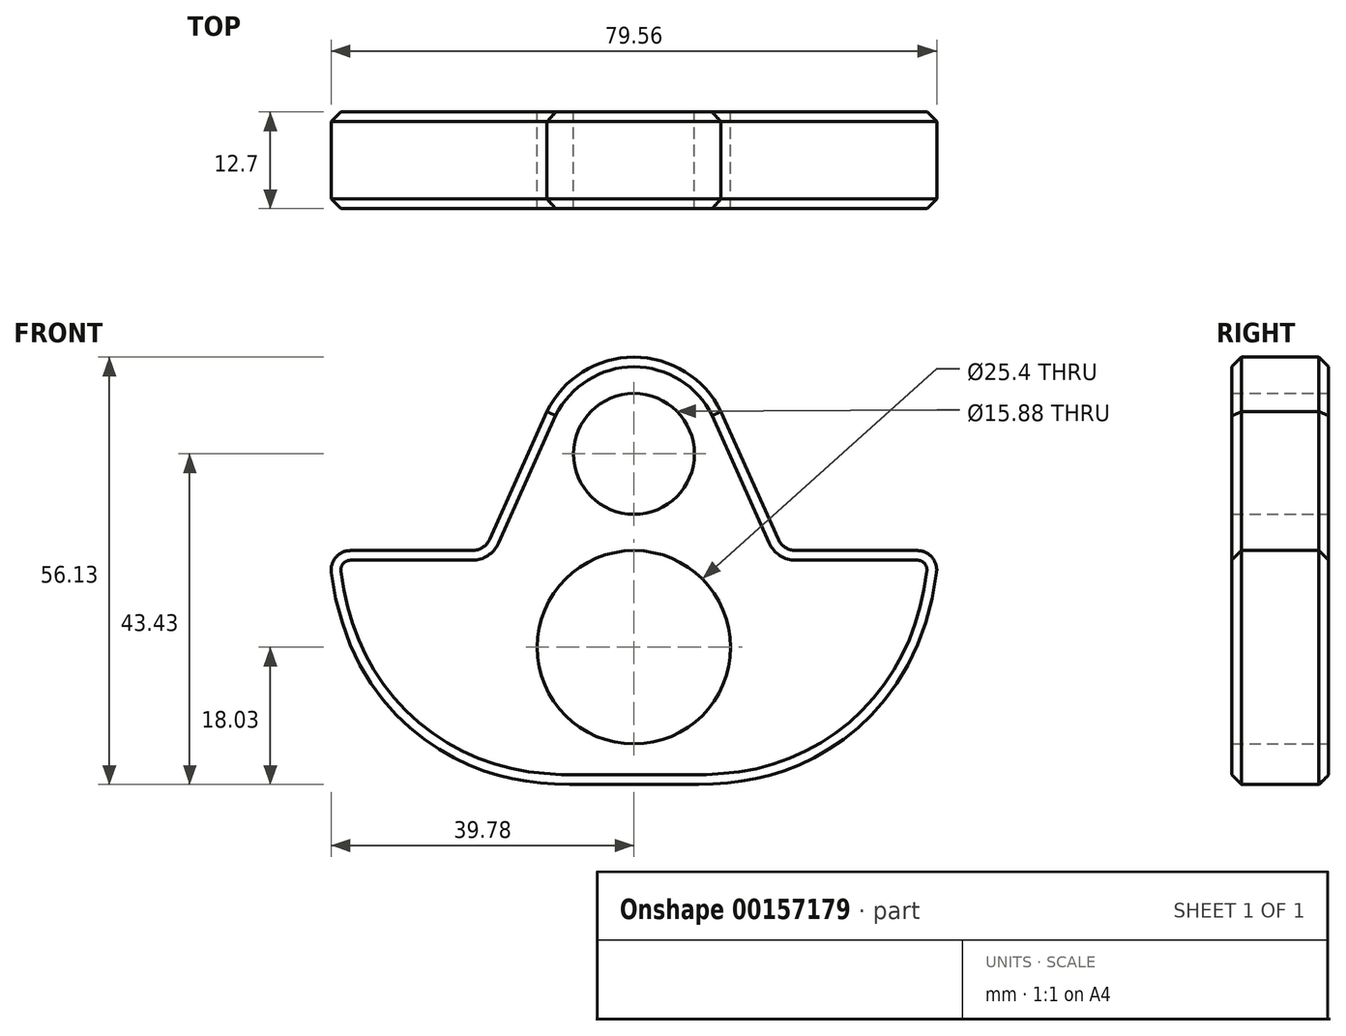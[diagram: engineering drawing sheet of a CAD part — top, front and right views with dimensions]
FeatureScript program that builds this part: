
annotation { "Feature Type Name" : "Feature", "Feature Type Description" : "" }
export const myFeature = defineFeature(function(context is Context, id is Id, definition is map)
    precondition{}
    {
        {
            var Q0;
            Q0=qCreatedBy(makeId("Front.planeOp"),FACE);
            var sketch = newSketch(context, id + "F0", { "sketchPlane" : qUnion([Q0])});
            skCircle(sketch, "E0", {"center": v(0, 0) * mm, "radius": 12.7 * mm});
            skLineSegment(sketch, "E1", {"start": v(0, 0) * mm, "end": v(0, 25.4) * mm});
            skCircle(sketch, "E2", {"center": v(0, 25.4) * mm, "radius": 7.94 * mm});
            skFitSpline(sketch, "E3", {"points": [v(0, -18) * mm, v(20.39, -15.98) * mm, v(40.02, 12.7) * mm], "startDerivative": vector(55.15, 0.13) * mm, "endDerivative": vector(5.47, 90.1) * mm});
            skLineSegment(sketch, "E4", {"start": v(37.24, 12.7) * mm, "end": v(21.26, 12.7) * mm});
            skArc(sketch, "E5", {"start": v(11.74, 30.24) * mm, "mid": v(0, 38.1) * mm, "end": v(-11.74, 30.24) * mm});
            skLineSegment(sketch, "E6", {"start": v(18.95, 14.2) * mm, "end": v(11.42, 30.96) * mm});
            skArc(sketch, "E7.filletArc", {"start": v(39.76, 9.84) * mm, "mid": v(39.14, 11.84) * mm, "end": v(37.24, 12.7) * mm});
            skPoint(sketch, "E8.visualSharp", {"position": v(19.62, 12.7) * mm});
            skArc(sketch, "E8.filletArc", {"start": v(18.95, 14.2) * mm, "mid": v(19.88, 13.1) * mm, "end": v(21.26, 12.7) * mm});
            skLineSegment(sketch, "E9.MirrorCS", {"start": v(-18.95, 14.2) * mm, "end": v(-11.42, 30.96) * mm});
            skLineSegment(sketch, "E10.MirrorCS", {"start": v(-37.24, 12.7) * mm, "end": v(-21.26, 12.7) * mm});
            skArc(sketch, "E11.MirrorCS", {"start": v(-18.95, 14.2) * mm, "mid": v(-19.88, 13.1) * mm, "end": v(-21.26, 12.7) * mm});
            skArc(sketch, "E12.MirrorCS", {"start": v(-39.76, 9.84) * mm, "mid": v(-39.14, 11.84) * mm, "end": v(-37.24, 12.7) * mm});
            skFitSpline(sketch, "E13.MirrorCS", {"points": [v(0, -18) * mm, v(-20.39, -15.98) * mm, v(-40.02, 12.7) * mm], "startDerivative": vector(-55.15, 0.13) * mm, "endDerivative": vector(-5.47, 90.1) * mm});
            skSolve(sketch);
        }
        {
            var Q0;
            Q0=makeQuery(id+"F0.imprint","IMPRINT",FACE,{"disambiguationData":[TD([[makeQuery(id+"F0.imprint","IMPRINT",EDGE,{"derivedFrom":sQuery(id+"F0.wireOp",EDGE,"E0")}),-1.0]])]});
            extrude(context, id + "F1", {"entities" : qUnion([Q0]), "depth" : 12.7 * mm});
        }
        {
            var Q0;
            Q0=makeQuery(id+"F1.opExtrude","CAP_EDGE",EDGE,{"disambiguationData":[OSD([sQuery(id+"F0.wireOp",EDGE,"E10.MirrorCS")])],"isStart":false});
            var Q1;
            Q1=makeQuery(id+"F1.opExtrude","CAP_EDGE",EDGE,{"disambiguationData":[OSD([sQuery(id+"F0.wireOp",EDGE,"E5")])],"isStart":false});
            var Q2;
            Q2=makeQuery(id+"F1.opExtrude","CAP_EDGE",EDGE,{"disambiguationData":[OSD([sQuery(id+"F0.wireOp",EDGE,"E6")])],"isStart":false});
            chamfer(context, id + "F2", {"entities" : qUnion([Q0, Q1, Q2]), "width" : 1.27 * mm, "tangentPropagation" : true});
        }
        {
            var Q0;
            Q0=makeQuery(id+"F1.opExtrude","CAP_EDGE",EDGE,{"disambiguationData":[OSD([sQuery(id+"F0.wireOp",EDGE,"E5")])],"isStart":true});
            var Q1;
            Q1=makeQuery(id+"F1.opExtrude","CAP_EDGE",EDGE,{"disambiguationData":[OSD([sQuery(id+"F0.wireOp",EDGE,"E9.MirrorCS")])],"isStart":true});
            var Q2;
            Q2=makeQuery(id+"F1.opExtrude","CAP_EDGE",EDGE,{"disambiguationData":[OSD([sQuery(id+"F0.wireOp",EDGE,"E11.MirrorCS")])],"isStart":true});
            var Q3;
            Q3=makeQuery(id+"F1.opExtrude","CAP_EDGE",EDGE,{"disambiguationData":[OSD([sQuery(id+"F0.wireOp",EDGE,"E10.MirrorCS")])],"isStart":true});
            var Q4;
            Q4=makeQuery(id+"F1.opExtrude","CAP_EDGE",EDGE,{"disambiguationData":[OSD([sQuery(id+"F0.wireOp",EDGE,"E12.MirrorCS")])],"isStart":true});
            var Q5;
            Q5=makeQuery(id+"F1.opExtrude","CAP_EDGE",EDGE,{"disambiguationData":[OSD([sQuery(id+"F0.wireOp",EDGE,"E13.MirrorCS")])],"isStart":true});
            var Q6;
            Q6=makeQuery(id+"F1.opExtrude","CAP_EDGE",EDGE,{"disambiguationData":[OSD([sQuery(id+"F0.wireOp",EDGE,"E3")])],"isStart":true});
            var Q7;
            Q7=makeQuery(id+"F1.opExtrude","CAP_EDGE",EDGE,{"disambiguationData":[OSD([sQuery(id+"F0.wireOp",EDGE,"E7.filletArc")])],"isStart":true});
            var Q8;
            Q8=makeQuery(id+"F1.opExtrude","CAP_EDGE",EDGE,{"disambiguationData":[OSD([sQuery(id+"F0.wireOp",EDGE,"E4")])],"isStart":true});
            var Q9;
            Q9=makeQuery(id+"F1.opExtrude","CAP_EDGE",EDGE,{"disambiguationData":[OSD([sQuery(id+"F0.wireOp",EDGE,"E8.filletArc")])],"isStart":true});
            var Q10;
            Q10=makeQuery(id+"F1.opExtrude","CAP_EDGE",EDGE,{"disambiguationData":[OSD([sQuery(id+"F0.wireOp",EDGE,"E6")])],"isStart":true});
            chamfer(context, id + "F3", {"entities" : qUnion([Q0, Q1, Q2, Q3, Q4, Q5, Q6, Q7, Q8, Q9, Q10]), "width" : 1.27 * mm, "tangentPropagation" : true});
        }
    });
